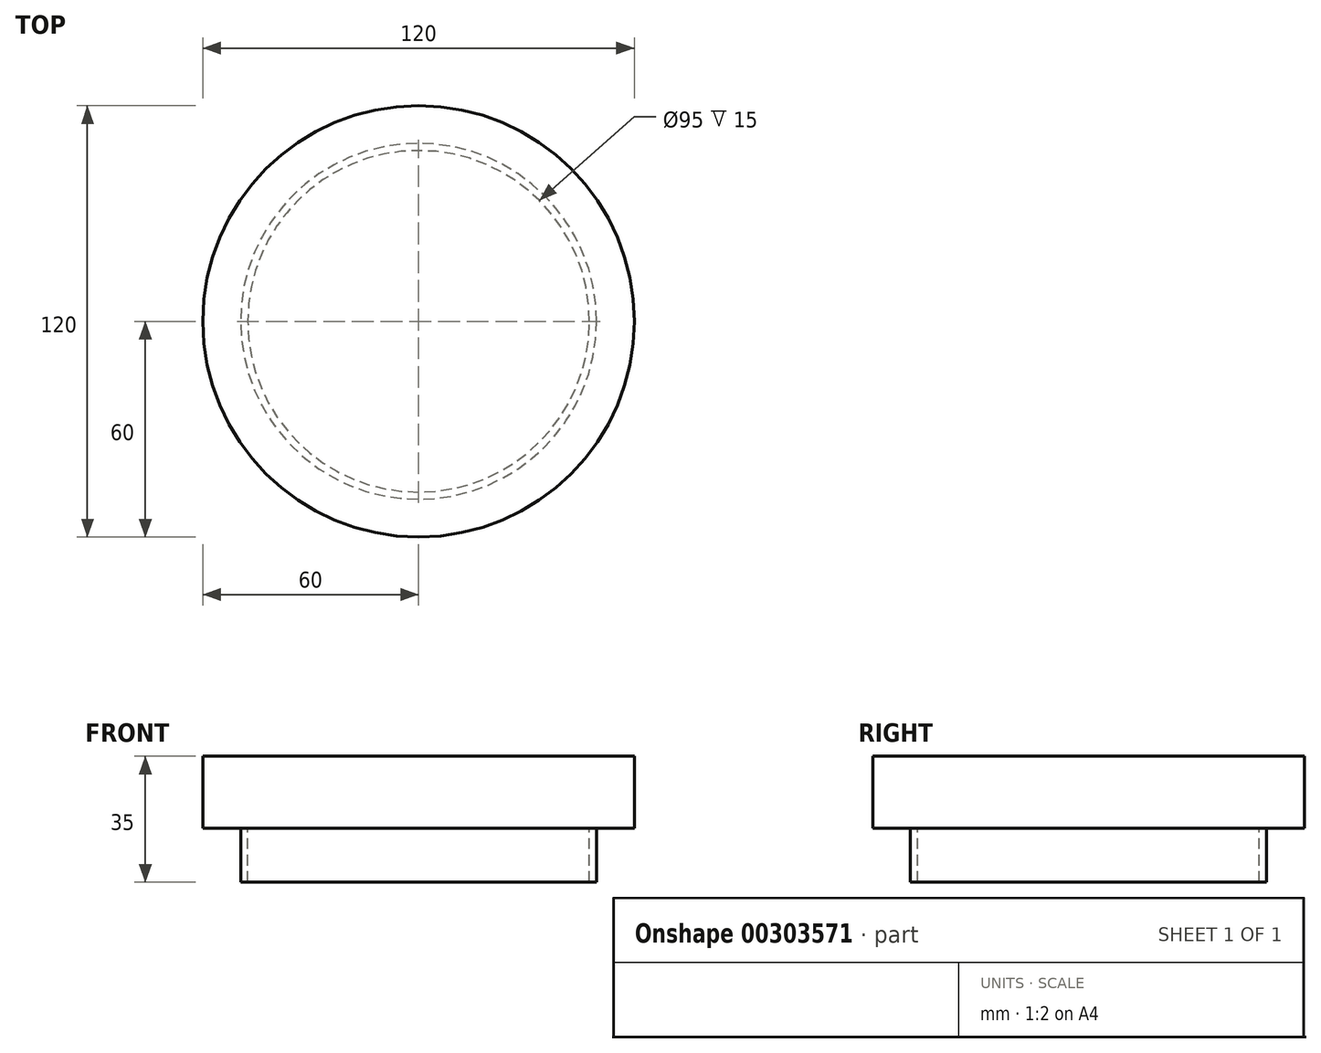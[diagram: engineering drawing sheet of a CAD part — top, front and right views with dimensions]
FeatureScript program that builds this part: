
annotation { "Feature Type Name" : "Feature", "Feature Type Description" : "" }
export const myFeature = defineFeature(function(context is Context, id is Id, definition is map)
    precondition{}
    {
        {
            var Q0;
            Q0=qCreatedBy(makeId("Top.planeOp"),FACE);
            var sketch = newSketch(context, id + "F0", { "sketchPlane" : qUnion([Q0])});
            skCircle(sketch, "E0", {"center": v(0, 0) * mm, "radius": 60 * mm});
            skSolve(sketch);
        }
        {
            var Q0;
            Q0=makeQuery(id+"F0.imprint","IMPRINT",FACE,{"disambiguationData":[TD([[makeQuery(id+"F0.imprint","IMPRINT",EDGE,{"derivedFrom":sQuery(id+"F0.wireOp",EDGE,"E0")}),1.0]])]});
            extrude(context, id + "F1", {"entities" : qUnion([Q0]), "depth" : 20 * mm});
        }
        {
            var Q0;
            Q0=makeQuery(id+"F1.opExtrude","CAP_FACE",FACE,{"disambiguationData":[OSD([sQuery(id+"F0.wireOp",EDGE,"E0")])],"isStart":true});
            var sketch = newSketch(context, id + "F2", { "sketchPlane" : qUnion([Q0])});
            skCircle(sketch, "E1", {"center": v(0, 0) * mm, "radius": 49.5 * mm});
            skCircle(sketch, "E2", {"center": v(0, 0) * mm, "radius": 47.5 * mm});
            skSolve(sketch);
        }
        {
            var Q0;
            Q0=makeQuery(id+"F2.imprint","IMPRINT",FACE,{"disambiguationData":[TD([[makeQuery(id+"F2.imprint","IMPRINT",EDGE,{"derivedFrom":sQuery(id+"F2.wireOp",EDGE,"E1")}),1.0]])]});
            extrude(context, id + "F3", {"entities" : qUnion([Q0]), "operationType" : NewBodyOperationType.ADD, "depth" : 15 * mm});
        }
    });
